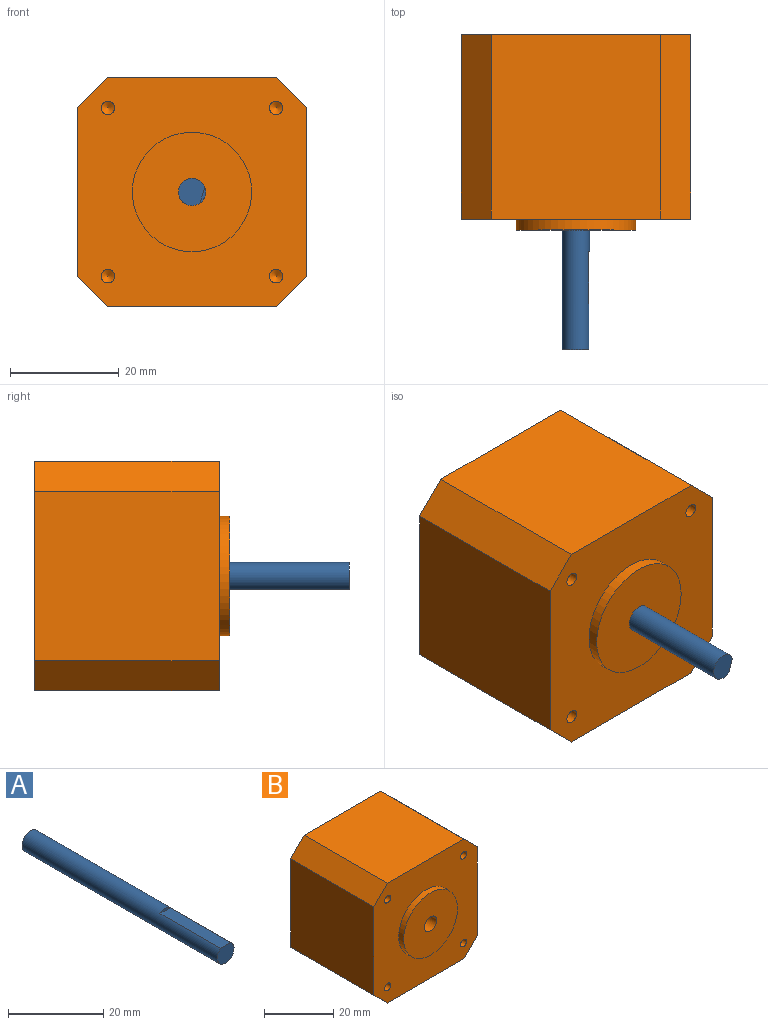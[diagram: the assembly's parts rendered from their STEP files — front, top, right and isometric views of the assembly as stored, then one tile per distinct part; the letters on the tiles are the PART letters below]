
ASSEMBLY  parts=2 mates=1
PART A: 5 faces, bbox 5x58x5 mm
  f0: cylinder r=2.5mm len=58mm, axis (0,1,0), area 853.1mm2, adj f1,f2,f3,f4
  f1: plane 5x4.5mm, normal (0,-1,0), area 18.6mm2, adj f0,f3
  f2: plane 5x5mm, normal (0,1,0), area 19.6mm2, adj f0
  f3: plane 18x3mm, normal (0,0,1), area 54mm2, adj f0,f1,f4
  f4: plane 3x0.5mm, normal (0,-1,0), area 1mm2, adj f0,f3
PART B: 21 faces, bbox 42.3x36x42.3 mm
  f0: plane 34x5.53mm, normal (-0.71,0,0.71), area 265.9mm2, adj f1,f7,f9,f10
  f1: plane 34x31.24mm, normal (-1,0,0), area 1062.1mm2, adj f0,f2,f9,f10
  f2: plane 34x5.53mm, normal (-0.71,0,-0.71), area 265.9mm2, adj f1,f3,f9,f10
  f3: plane 34x31.24mm, normal (0,0,-1), area 1062.1mm2, adj f2,f4,f9,f10
  f4: plane 34x5.53mm, normal (0.71,0,-0.71), area 265.9mm2, adj f3,f5,f9,f10
  f5: plane 34x31.24mm, normal (1,0,0), area 1062.1mm2, adj f4,f6,f9,f10
  f6: plane 34x5.53mm, normal (0.71,0,0.71), area 265.9mm2, adj f5,f7,f9,f10
  f7: plane 34x31.24mm, normal (0,0,1), area 1062.1mm2, adj f0,f6,f9,f10
  f8: cylinder r=2.5mm len=36mm, axis (0,-1,0), area 565.5mm2, adj f9,f12
  f9: plane 42.3x42.3mm, normal (0,1,0), area 1708.5mm2, adj f0,f1,f2,f3,f4,f5,f6,f7
  f10: plane 42.3x42.3mm, normal (0,-1,0), area 1328.4mm2, adj f0,f1,f2,f3,f4,f5,f6,f7
  f11: cylinder r=11mm len=22mm, axis (0,1,0), area 138.2mm2, adj f10,f12
  f12: plane 22x22mm, normal (0,-1,0), area 360.5mm2, adj f8,f11
  f13: cone r=0mm half-angle=59deg, axis (0,-1,0), area 5.7mm2, adj f14
  f14: cylinder r=1.25mm len=6mm, axis (0,-1,0), area 47.1mm2, adj f10,f13
  f15: cone r=0mm half-angle=59deg, axis (0,-1,0), area 5.7mm2, adj f16
  f16: cylinder r=1.25mm len=6mm, axis (0,-1,0), area 47.1mm2, adj f10,f15
  f17: cone r=0mm half-angle=59deg, axis (0,-1,0), area 5.7mm2, adj f18
  f18: cylinder r=1.25mm len=6mm, axis (0,-1,0), area 47.1mm2, adj f10,f17
  f19: cone r=0mm half-angle=59deg, axis (0,-1,0), area 5.7mm2, adj f20
  f20: cylinder r=1.25mm len=6mm, axis (0,-1,0), area 47.1mm2, adj f10,f19
PLACE A rot(axis=(0,1,0),108.4deg) t=(0,0,0)mm
PLACE B at identity fixed
MATE revolute A.f0 <-> B.f8  axis (0,1,0) through (0,34,0)mm
